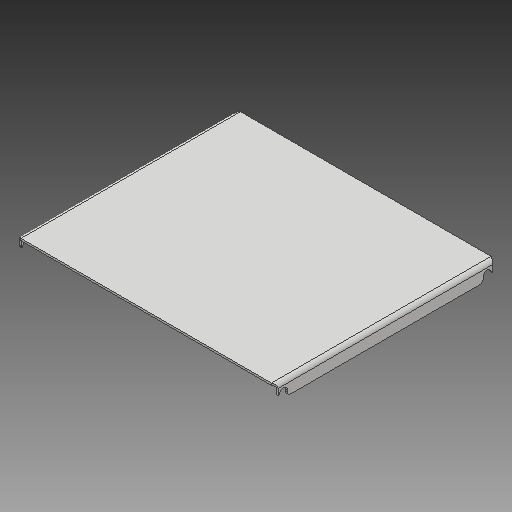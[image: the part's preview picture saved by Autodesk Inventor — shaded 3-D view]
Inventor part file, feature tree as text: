
AUTODESK INVENTOR PART (.ipt)
format: ipt  version: 2018 (Build 220112000, 112)  size: 236,544 bytes
history: native  units: mm
features: other x11, sketch x3, extrude x1, projected_geometry x1, reference x1
ambient origin geometry x8: Origin, YZ Plane, XZ Plane, XY Plane, X Axis, Y Axis, Z Axis, Center Point
bodies: Volumenkörper1 (feature_tree)
feature tree (17):
  other  "Fläche1"
  other  "Lasche4"
  other  "Eckenrundung1"
  extrude  "Extrusion2"  Depth=219.8mm
  sketch  "Skizze1"  dims[d0=258.8mm d1=219.8mm]
  other  "Grobblech1"
  sketch  "Skizze6"  dims[d2=2.0mm]
  other  "Grobblech5"
  other  "Biegung4"
  other  "Ecke4"
  sketch  "Skizze7"  dims[d41=3.0mm d42=2.0mm d43=1.0mm d44=4.0mm d45=2.0mm d46=15.0mm d47=90.0deg d48=2.0mm d49=8.0mm d50=2.0mm d51=2.0mm d52=3.0mm d53=0.05mm d54=5.0mm d55=3.0mm d56=1.0mm d57=10.0mm d58=0.0mm]
  projected_geometry  "Projizierte Kontur1"
  reference  "Referenz1"
  parser-record x1  (decoder bookkeeping rows leaked as tree rows — omitted from the tree; the rows remain in map.json)
  other  "Montiert.iam"
  other  "DIN 433-1 A 4,3:1"
  other  "Definition1"
note: 1 file-system path scrubbed to <path> (originals preserved in map.json)
